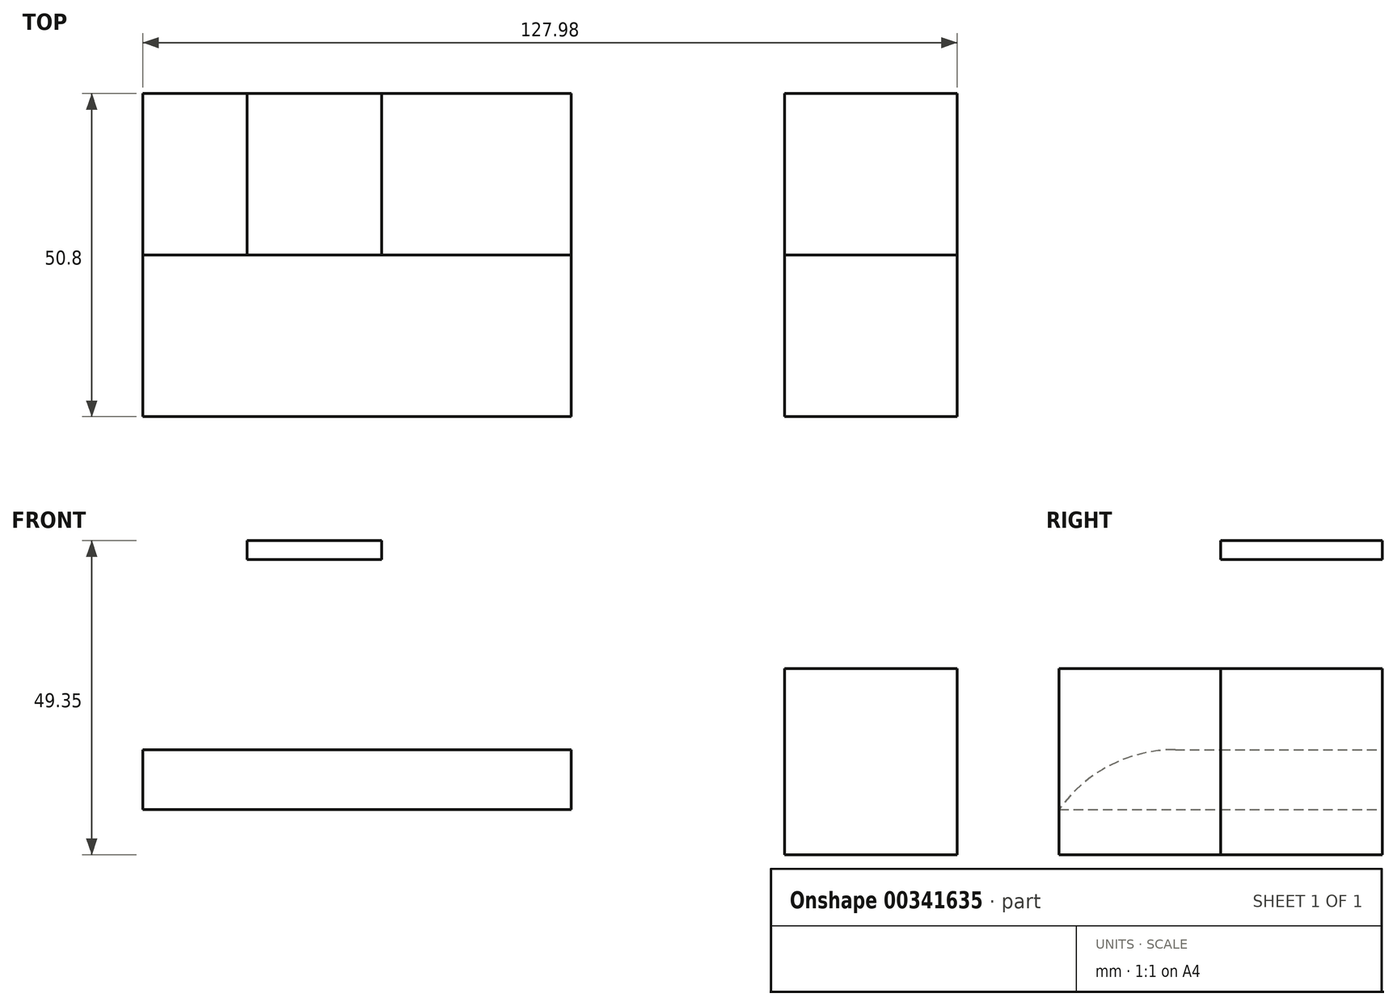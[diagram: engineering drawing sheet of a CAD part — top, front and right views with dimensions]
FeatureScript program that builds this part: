
annotation { "Feature Type Name" : "Feature", "Feature Type Description" : "" }
export const myFeature = defineFeature(function(context is Context, id is Id, definition is map)
    precondition{}
    {
        {
            var Q0;
            Q0=qCreatedBy(makeId("Front.planeOp"),FACE);
            var sketch = newSketch(context, id + "F0", { "sketchPlane" : qUnion([Q0])});
            skLineSegment(sketch, "E0.bottom", {"start": v(-67.34, -57.05) * mm, "end": v(0, -57.05) * mm});
            skLineSegment(sketch, "E0.top", {"start": v(-67.34, -47.64) * mm, "end": v(0, -47.64) * mm});
            skLineSegment(sketch, "E0.left", {"start": v(-67.34, -57.05) * mm, "end": v(-67.34, -47.64) * mm});
            skLineSegment(sketch, "E0.right", {"start": v(0, -57.05) * mm, "end": v(0, -47.64) * mm});
            skLineSegment(sketch, "E1.bottom", {"start": v(-29.8, -14.8) * mm, "end": v(-50.95, -14.8) * mm});
            skLineSegment(sketch, "E1.top", {"start": v(-29.8, -17.76) * mm, "end": v(-50.95, -17.76) * mm});
            skLineSegment(sketch, "E1.left", {"start": v(-29.8, -14.8) * mm, "end": v(-29.8, -17.76) * mm});
            skLineSegment(sketch, "E1.right", {"start": v(-50.95, -14.8) * mm, "end": v(-50.95, -17.76) * mm});
            skLineSegment(sketch, "E2.bottom", {"start": v(33.53, -64.15) * mm, "end": v(60.64, -64.15) * mm});
            skLineSegment(sketch, "E2.top", {"start": v(33.53, -34.9) * mm, "end": v(60.64, -34.9) * mm});
            skLineSegment(sketch, "E2.left", {"start": v(33.53, -64.15) * mm, "end": v(33.53, -34.9) * mm});
            skLineSegment(sketch, "E2.right", {"start": v(60.64, -64.15) * mm, "end": v(60.64, -34.9) * mm});
            skSolve(sketch);
        }
        {
            var Q0;
            Q0 = qSketchRegion(id + "F0", true);
            extrude(context, id + "F1", {"entities" : qUnion([Q0]), "depth" : 25.4 * mm});
        }
        {
            var Q0;
            Q0=makeQuery(id+"F1.opExtrude","CAP_FACE",FACE,{"disambiguationData":[OSD([sQuery(id+"F0.wireOp",EDGE,"E2.bottom"),sQuery(id+"F0.wireOp",EDGE,"E2.top"),sQuery(id+"F0.wireOp",EDGE,"E2.left"),sQuery(id+"F0.wireOp",EDGE,"E2.right")])],"isStart":false});
            var Q1;
            Q1=makeQuery(id+"F1.opExtrude","CAP_FACE",FACE,{"disambiguationData":[OSD([sQuery(id+"F0.wireOp",EDGE,"E0.bottom"),sQuery(id+"F0.wireOp",EDGE,"E0.top"),sQuery(id+"F0.wireOp",EDGE,"E0.left"),sQuery(id+"F0.wireOp",EDGE,"E0.right")])],"isStart":false});
            extrude(context, id + "F2", {"entities" : qUnion([Q0, Q1]), "depth" : 25.4 * mm});
        }
        {
            var Q0;
            Q0=makeQuery(id+"F2.opExtrude","CAP_EDGE",EDGE,{"disambiguationData":[OSD([sQuery(id+"F0.wireOp",EDGE,"E0.top")])],"isStart":false});
            fillet(context, id + "F3", {"entities" : qUnion([Q0]), "radius" : 22.44 * mm, "tangentPropagation" : true, "allowEdgeOverflow" : false});
        }
    });
